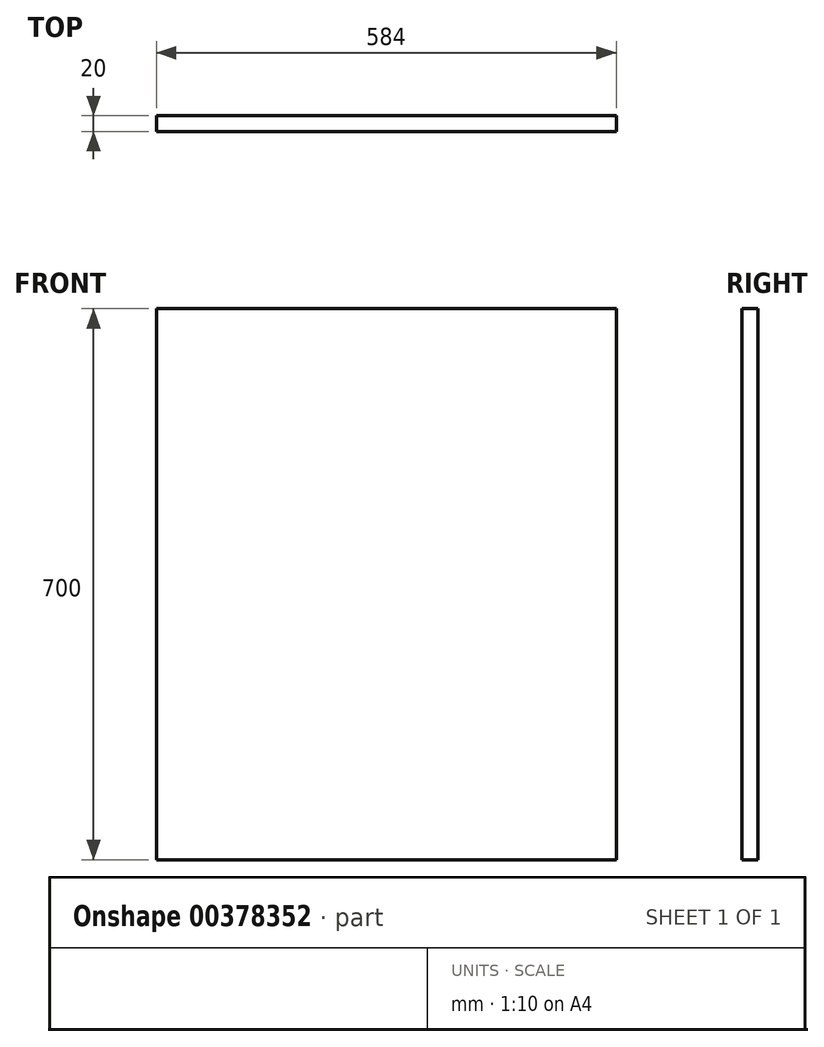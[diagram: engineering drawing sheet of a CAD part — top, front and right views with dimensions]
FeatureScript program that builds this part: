
annotation { "Feature Type Name" : "Feature", "Feature Type Description" : "" }
export const myFeature = defineFeature(function(context is Context, id is Id, definition is map)
    precondition{}
    {
        {
            var Q0;
            Q0=qCreatedBy(makeId("Front.planeOp"),FACE);
            var sketch = newSketch(context, id + "F0", { "sketchPlane" : qUnion([Q0])});
            skLineSegment(sketch, "E0.bottom", {"start": v(292, 350) * mm, "end": v(-292, 350) * mm});
            skLineSegment(sketch, "E0.top", {"start": v(292, -350) * mm, "end": v(-292, -350) * mm});
            skLineSegment(sketch, "E0.left", {"start": v(292, 350) * mm, "end": v(292, -350) * mm});
            skLineSegment(sketch, "E0.right", {"start": v(-292, 350) * mm, "end": v(-292, -350) * mm});
            skPoint(sketch, "E0.middle", {"position": v(0, 0) * mm});
            skSolve(sketch);
        }
        {
            var Q0;
            Q0 = qSketchRegion(id + "F0", true);
            extrude(context, id + "F1", {"entities" : qUnion([Q0]), "depth" : 20 * mm});
        }
    });
